# Revit family: Taylor_Entrance_2_Panel_High_Def_Large
name_source: partatom
category: Doors
units: mm (PartAtom-declared; Revit-internal decimal feet)

## family parameters
Always vertical = Yes
Classification Number = 23.30.10.00
Cut with Voids When Loaded = No
Host = Wall
Room Calculation Point = No
Shared = No

## types (2) — shared parameters
Analytic Construction = <None>
Description = 2 panel high def (HD) large embossment option for steel doors
Door Finish = Door Finish - Grey Paintable Primer
Door Frame Finish = Material - Door - Frame
Function = Interior
Height = 6' - 8"
Manufacturer = Taylor Entrance Systems
Manufacturer Fax = 800-252-5468
Manufacturer Website = http://www.taylordoor.com
Rough Height = 6' - 10"
Rough Width = 3' - 4"
Sales Information = http://www.taylordoor.com
Specification = https://charrette.arcat.com
Thickness = 0' - 1 3/4"
Wall Closure = By host
Width = 3' - 0"

## per-type parameters (varying)
| type | Model | Planks |
| High Def Arch | 2 Panel High Def Arch | No |
| High Def Planks | 2 Panel High Def Planks | Yes |

## geometry (parser evidence)
native form markers: Sweep x5
no freeform markers — native parametric forms only
